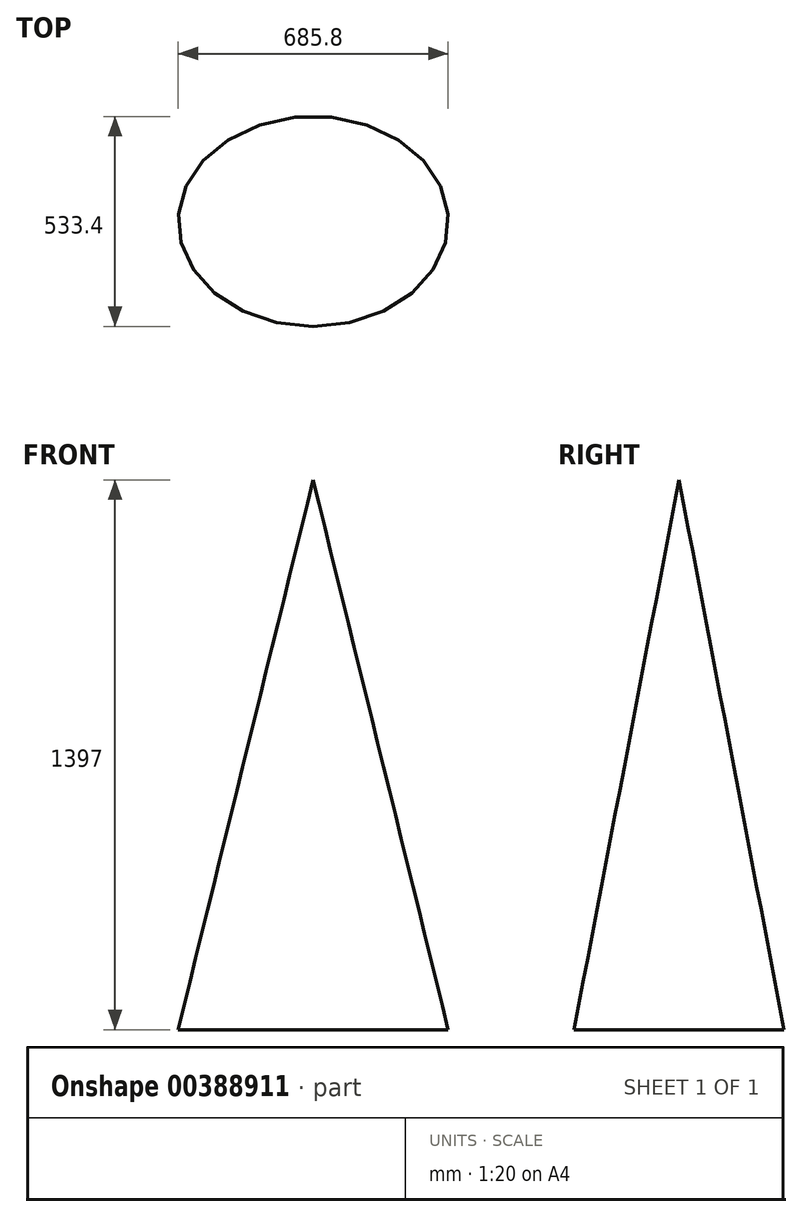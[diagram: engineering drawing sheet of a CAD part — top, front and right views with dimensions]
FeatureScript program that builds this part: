
annotation { "Feature Type Name" : "Feature", "Feature Type Description" : "" }
export const myFeature = defineFeature(function(context is Context, id is Id, definition is map)
    precondition{}
    {
        {
            var Q0;
            Q0=qCreatedBy(makeId("Top.planeOp"),FACE);
            var sketch = newSketch(context, id + "F0", { "sketchPlane" : qUnion([Q0])});
            skEllipse(sketch, "E0", {"center": v(0, 0) * mm, "majorRadius": 342.9 * mm, "minorRadius": 266.7 * mm, "majorAxis": v(1, 0)});
            skSolve(sketch);
        }
        {
            var Q0;
            Q0=qCreatedBy(makeId("Top.planeOp"),FACE);
            cPlane(context, id + "F1", {"entities" : qUnion([Q0]), "cplaneType" : CPlaneType.OFFSET, "offset" : 1397 * mm, "width" : 152.4 * mm, "height" : 152.4 * mm});
        }
        {
            var Q0;
            Q0=qCreatedBy(id+"F1.planeOp",FACE);
            var sketch = newSketch(context, id + "F2", { "sketchPlane" : qUnion([Q0])});
            skPoint(sketch, "E1", {"position": v(0, 0) * mm});
            skSolve(sketch);
        }
        {
            var Q0;
            Q0=makeQuery(id+"F0.imprint","IMPRINT",FACE,{"disambiguationData":[TD([[makeQuery(id+"F0.imprint","IMPRINT",EDGE,{"derivedFrom":sQuery(id+"F0.wireOp",EDGE,"E0")}),1.0]])]});
            var Q1;
            Q1=sQuery(id+"F2.wireOp",VERTEX,"E1");
            loft(context, id + "F3", {"sheetProfilesArray" : [{ "sheetProfileEntities" : qUnion([Q0]) }, { "sheetProfileEntities" : qUnion([Q1]) }]});
        }
    });
